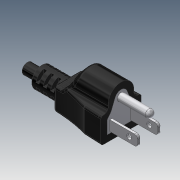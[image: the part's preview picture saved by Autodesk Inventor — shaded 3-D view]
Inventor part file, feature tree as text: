
AUTODESK INVENTOR PART (.ipt)
format: ipt  version: 2020.3 (Build 243373000, 373)  size: 411,648 bytes
history: mixed  units: in
note: dims shown in document units (in); Inventor stores cm internally (conversion verified against a paired STEP export)
features: other x2, revolve x1, chamfer x1, imported_body x1
ambient origin geometry x8: Origin, YZ Plane, XZ Plane, XY Plane, X Axis, Y Axis, Z Axis, Center Point
bodies: Solid1 (imported_parasolid), Solid2 (imported_parasolid), Solid3 (imported_parasolid), Solid4 (imported_parasolid)
feature tree (5):
  other  "Boss-Extrude3"
  revolve  "Revolve1"  [1 undecoded]
  other  "Boss-Extrude5"
  chamfer  "Chamfer1"  [1 undecoded]
  imported_body  NMx_Import_Brep_tag  [imported B-rep: ~18 faces, bbox_mm=[30.25, 17.35, 6.95]]
note: 2 required parameter values undecoded (feature->parameter linkage not recoverable at this tier; creation-order binding heuristic only, values carry confidence <= 0.55)
